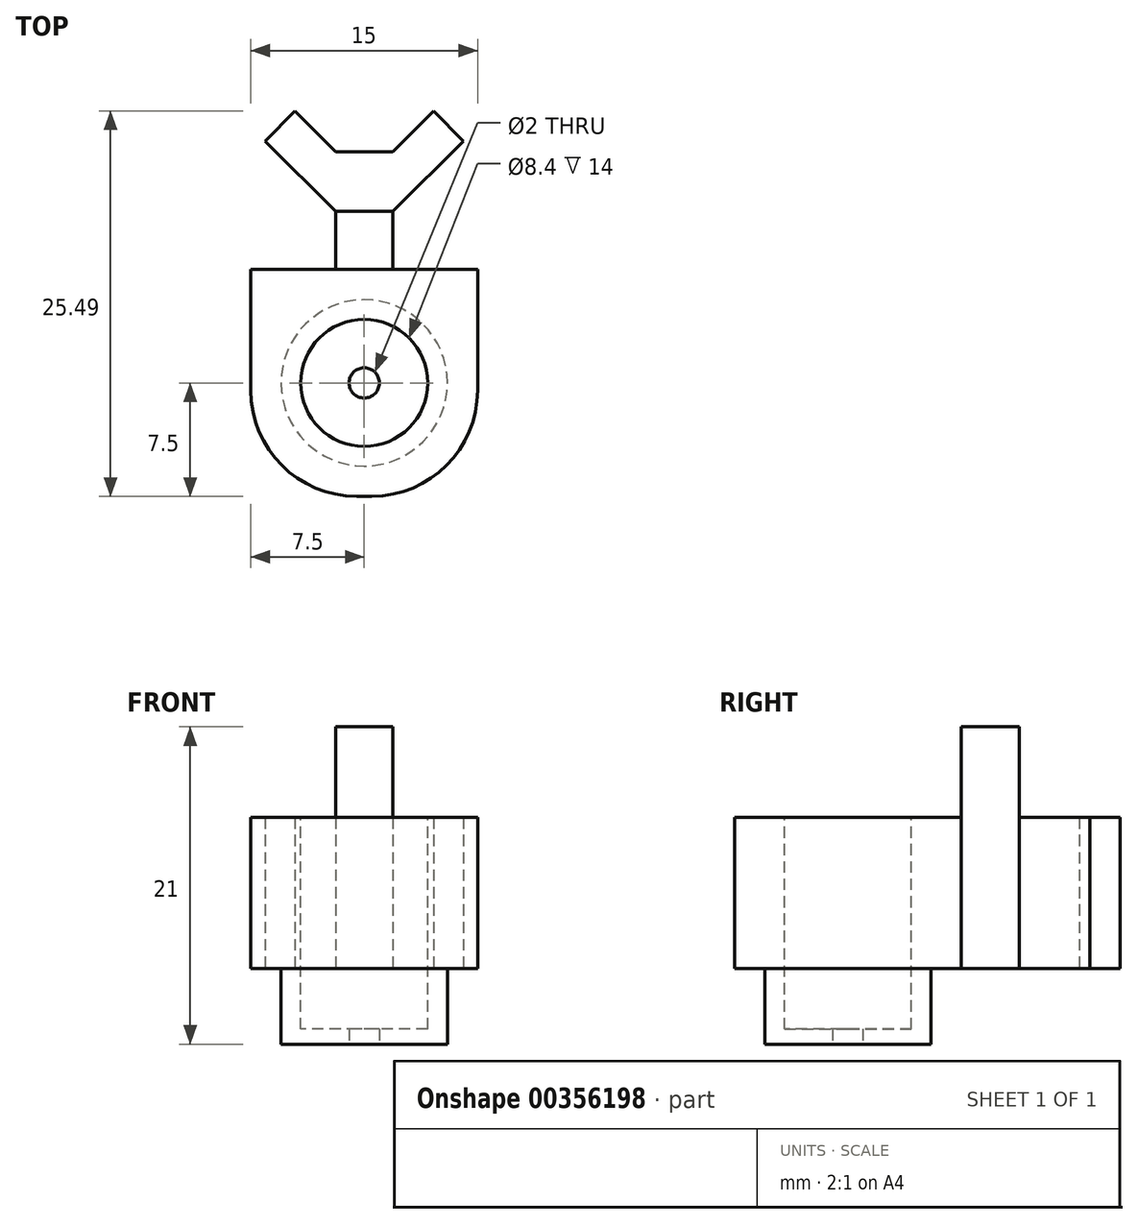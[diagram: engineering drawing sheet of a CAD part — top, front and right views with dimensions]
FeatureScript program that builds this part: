
annotation { "Feature Type Name" : "Feature", "Feature Type Description" : "" }
export const myFeature = defineFeature(function(context is Context, id is Id, definition is map)
    precondition{}
    {
        {
            var Q0;
            Q0=qCreatedBy(makeId("Top.planeOp"),FACE);
            var sketch = newSketch(context, id + "F0", { "sketchPlane" : qUnion([Q0])});
            skLineSegment(sketch, "E0.bottom", {"start": v(0, 0) * mm, "end": v(15, 0) * mm});
            skLineSegment(sketch, "E0.top", {"start": v(0, 15) * mm, "end": v(15, 15) * mm});
            skLineSegment(sketch, "E0.left", {"start": v(0, 0) * mm, "end": v(0, 15) * mm});
            skLineSegment(sketch, "E0.right", {"start": v(15, 0) * mm, "end": v(15, 15) * mm});
            skPoint(sketch, "E1", {"position": v(5.6, 15) * mm});
            skPoint(sketch, "E2", {"position": v(9.4, 15) * mm});
            skPoint(sketch, "E3", {"position": v(7.5, 15) * mm});
            skLineSegment(sketch, "E4", {"start": v(9.4, 15) * mm, "end": v(9.4, 22.8) * mm});
            skLineSegment(sketch, "E5", {"start": v(9.4, 22.8) * mm, "end": v(5.6, 22.8) * mm});
            skLineSegment(sketch, "E6", {"start": v(5.6, 15) * mm, "end": v(5.6, 22.8) * mm});
            skLineSegment(sketch, "E7", {"start": v(9.4, 22.8) * mm, "end": v(12.09, 25.49) * mm});
            skLineSegment(sketch, "E8", {"start": v(5.6, 22.8) * mm, "end": v(2.91, 25.49) * mm});
            skLineSegment(sketch, "E9", {"start": v(12.09, 25.49) * mm, "end": v(14.07, 23.5) * mm});
            skLineSegment(sketch, "E10", {"start": v(14.07, 23.5) * mm, "end": v(9.4, 18.84) * mm});
            skLineSegment(sketch, "E11", {"start": v(2.91, 25.49) * mm, "end": v(0.93, 23.5) * mm});
            skLineSegment(sketch, "E12", {"start": v(0.93, 23.5) * mm, "end": v(5.6, 18.84) * mm});
            skLineSegment(sketch, "E13", {"start": v(5.6, 18.84) * mm, "end": v(9.4, 18.84) * mm});
            skSolve(sketch);
        }
        {
            var Q0;
            Q0=makeQuery(id+"F0.imprint","IMPRINT",FACE,{"disambiguationData":[TD([[makeQuery(id+"F0.imprint","IMPRINT",EDGE,{"derivedFrom":sQuery(id+"F0.wireOp",EDGE,"E0.bottom")}),1.0]])]});
            var Q1;
            {var subQ5=sQuery(id+"F0.wireOp",EDGE,"E13");Q1=makeQuery(id+"F0.imprint","IMPRINT",FACE,{"disambiguationData":[TD([[makeQuery(id+"F0.imprint","IMPRINT",EDGE,{"derivedFrom":subQ5}),-1.0]])]});}
            var Q2;
            {var subQ0=sQuery(id+"F0.wireOp",EDGE,"E5");Q2=makeQuery(id+"F0.imprint","IMPRINT",FACE,{"disambiguationData":[TD([[makeQuery(id+"F0.imprint","IMPRINT",EDGE,{"derivedFrom":subQ0}),1.0]])]});}
            var Q3;
            {var subQ0=sQuery(id+"F0.wireOp",EDGE,"E7");Q3=makeQuery(id+"F0.imprint","IMPRINT",FACE,{"disambiguationData":[TD([[makeQuery(id+"F0.imprint","IMPRINT",EDGE,{"derivedFrom":subQ0}),-1.0]])]});}
            var Q4;
            {var subQ0=sQuery(id+"F0.wireOp",EDGE,"E8");Q4=makeQuery(id+"F0.imprint","IMPRINT",FACE,{"disambiguationData":[TD([[makeQuery(id+"F0.imprint","IMPRINT",EDGE,{"derivedFrom":subQ0}),1.0]])]});}
            extrude(context, id + "F1", {"entities" : qUnion([Q0, Q1, Q2, Q3, Q4]), "depth" : 10 * mm});
        }
        {
            var Q0;
            Q0=makeQuery(id+"F1.opExtrude","CAP_FACE",FACE,{"disambiguationData":[OSD([sQuery(id+"F0.wireOp",EDGE,"E0.bottom"),sQuery(id+"F0.wireOp",EDGE,"E0.top"),sQuery(id+"F0.wireOp",EDGE,"E0.left"),sQuery(id+"F0.wireOp",EDGE,"E0.right"),sQuery(id+"F0.wireOp",EDGE,"E4"),sQuery(id+"F0.wireOp",EDGE,"E5"),sQuery(id+"F0.wireOp",EDGE,"E6"),sQuery(id+"F0.wireOp",EDGE,"E7"),sQuery(id+"F0.wireOp",EDGE,"E8"),sQuery(id+"F0.wireOp",EDGE,"E9"),sQuery(id+"F0.wireOp",EDGE,"E10"),sQuery(id+"F0.wireOp",EDGE,"E11"),sQuery(id+"F0.wireOp",EDGE,"E12")])],"isStart":false});
            var sketch = newSketch(context, id + "F2", { "sketchPlane" : qUnion([Q0])});
            skLineSegment(sketch, "E14", {"start": v(5.6, 18.84) * mm, "end": v(9.4, 18.84) * mm});
            skLineSegment(sketch, "E15", {"start": v(9.4, 18.84) * mm, "end": v(9.4, 15) * mm});
            skLineSegment(sketch, "E16", {"start": v(9.4, 15) * mm, "end": v(5.6, 15) * mm});
            skLineSegment(sketch, "E17", {"start": v(5.6, 15) * mm, "end": v(5.6, 18.84) * mm});
            skSolve(sketch);
        }
        {
            var Q0;
            Q0 = qSketchRegion(id + "F2", true);
            extrude(context, id + "F3", {"entities" : qUnion([Q0]), "operationType" : NewBodyOperationType.ADD, "depth" : 6 * mm});
        }
        {
            var Q0;
            Q0=makeQuery(id+"F1.opExtrude","CAP_FACE",FACE,{"disambiguationData":[OSD([sQuery(id+"F0.wireOp",EDGE,"E0.bottom"),sQuery(id+"F0.wireOp",EDGE,"E0.top"),sQuery(id+"F0.wireOp",EDGE,"E0.left"),sQuery(id+"F0.wireOp",EDGE,"E0.right"),sQuery(id+"F0.wireOp",EDGE,"E4"),sQuery(id+"F0.wireOp",EDGE,"E5"),sQuery(id+"F0.wireOp",EDGE,"E6"),sQuery(id+"F0.wireOp",EDGE,"E7"),sQuery(id+"F0.wireOp",EDGE,"E8"),sQuery(id+"F0.wireOp",EDGE,"E9"),sQuery(id+"F0.wireOp",EDGE,"E10"),sQuery(id+"F0.wireOp",EDGE,"E11"),sQuery(id+"F0.wireOp",EDGE,"E12")])],"isStart":true});
            var sketch = newSketch(context, id + "F4", { "sketchPlane" : qUnion([Q0])});
            skPoint(sketch, "E18", {"position": v(7.5, 0) * mm});
            skPoint(sketch, "E19", {"position": v(0, -7.5) * mm});
            skCircle(sketch, "E20", {"center": v(7.5, -7.5) * mm, "radius": 5.5 * mm});
            skSolve(sketch);
        }
        {
            var Q0;
            Q0 = qSketchRegion(id + "F4", true);
            extrude(context, id + "F5", {"entities" : qUnion([Q0]), "operationType" : NewBodyOperationType.ADD, "depth" : 5 * mm});
        }
        {
            var Q0;
            Q0=makeQuery(id+"F5.opExtrude","CAP_FACE",FACE,{"disambiguationData":[OSD([sQuery(id+"F4.wireOp",EDGE,"E20")])],"isStart":false});
            var sketch = newSketch(context, id + "F6", { "sketchPlane" : qUnion([Q0])});
            skCircle(sketch, "E21", {"center": v(7.5, -7.5) * mm, "radius": 1 * mm});
            skSolve(sketch);
        }
        {
            var Q0;
            Q0 = qSketchRegion(id + "F6", true);
            extrude(context, id + "F7", {"entities" : qUnion([Q0]), "operationType" : NewBodyOperationType.REMOVE, "oppositeDirection" : true, "depth" : 25 * mm});
        }
        {
            var Q0;
            {var subQ0=sQuery(id+"F0.wireOp",EDGE,"E0.right");var subQ1=sQuery(id+"F0.wireOp",EDGE,"E0.top");var subQ2=sQuery(id+"F0.wireOp",EDGE,"E4");var subQ3=sQuery(id+"F0.wireOp",EDGE,"E0.left");var subQ4=sQuery(id+"F0.wireOp",EDGE,"E6");var subQ5=sQuery(id+"F0.wireOp",EDGE,"E0.bottom");Q0=makeQuery(id+"F3.boolean.opBoolean","SPLIT",FACE,{"disambiguationData":[TD([makeQuery(id+"F1.opExtrude","SWEPT_FACE",FACE,{"disambiguationData":[OSD([subQ5])]})])],"derivedFrom":makeQuery(id+"F1.opExtrude","CAP_FACE",FACE,{"disambiguationData":[OSD([subQ5,subQ1,subQ3,subQ0,subQ2,sQuery(id+"F0.wireOp",EDGE,"E5"),subQ4,sQuery(id+"F0.wireOp",EDGE,"E7"),sQuery(id+"F0.wireOp",EDGE,"E8"),sQuery(id+"F0.wireOp",EDGE,"E9"),sQuery(id+"F0.wireOp",EDGE,"E10"),sQuery(id+"F0.wireOp",EDGE,"E11"),sQuery(id+"F0.wireOp",EDGE,"E12")])],"isStart":false})});}
            var sketch = newSketch(context, id + "F8", { "sketchPlane" : qUnion([Q0])});
            skCircle(sketch, "E22", {"center": v(7.5, 7.5) * mm, "radius": 4.2 * mm});
            skSolve(sketch);
        }
        {
            var Q0;
            Q0 = qSketchRegion(id + "F8", true);
            extrude(context, id + "F9", {"entities" : qUnion([Q0]), "operationType" : NewBodyOperationType.REMOVE, "oppositeDirection" : true, "depth" : 14 * mm});
        }
        {
            var Q0;
            Q0=makeQuery(id+"F1.opExtrude","SWEPT_EDGE",EDGE,{"disambiguationData":[OSD([sQuery(id+"F0.wireOp",EDGE,"E0.bottom"),sQuery(id+"F0.wireOp",EDGE,"E0.right")])]});
            var Q1;
            Q1=makeQuery(id+"F1.opExtrude","SWEPT_EDGE",EDGE,{"disambiguationData":[OSD([sQuery(id+"F0.wireOp",EDGE,"E0.bottom"),sQuery(id+"F0.wireOp",EDGE,"E0.left")])]});
            fillet(context, id + "F10", {"entities" : qUnion([Q0, Q1]), "radius" : 7 * mm, "tangentPropagation" : true, "allowEdgeOverflow" : false});
        }
    });
